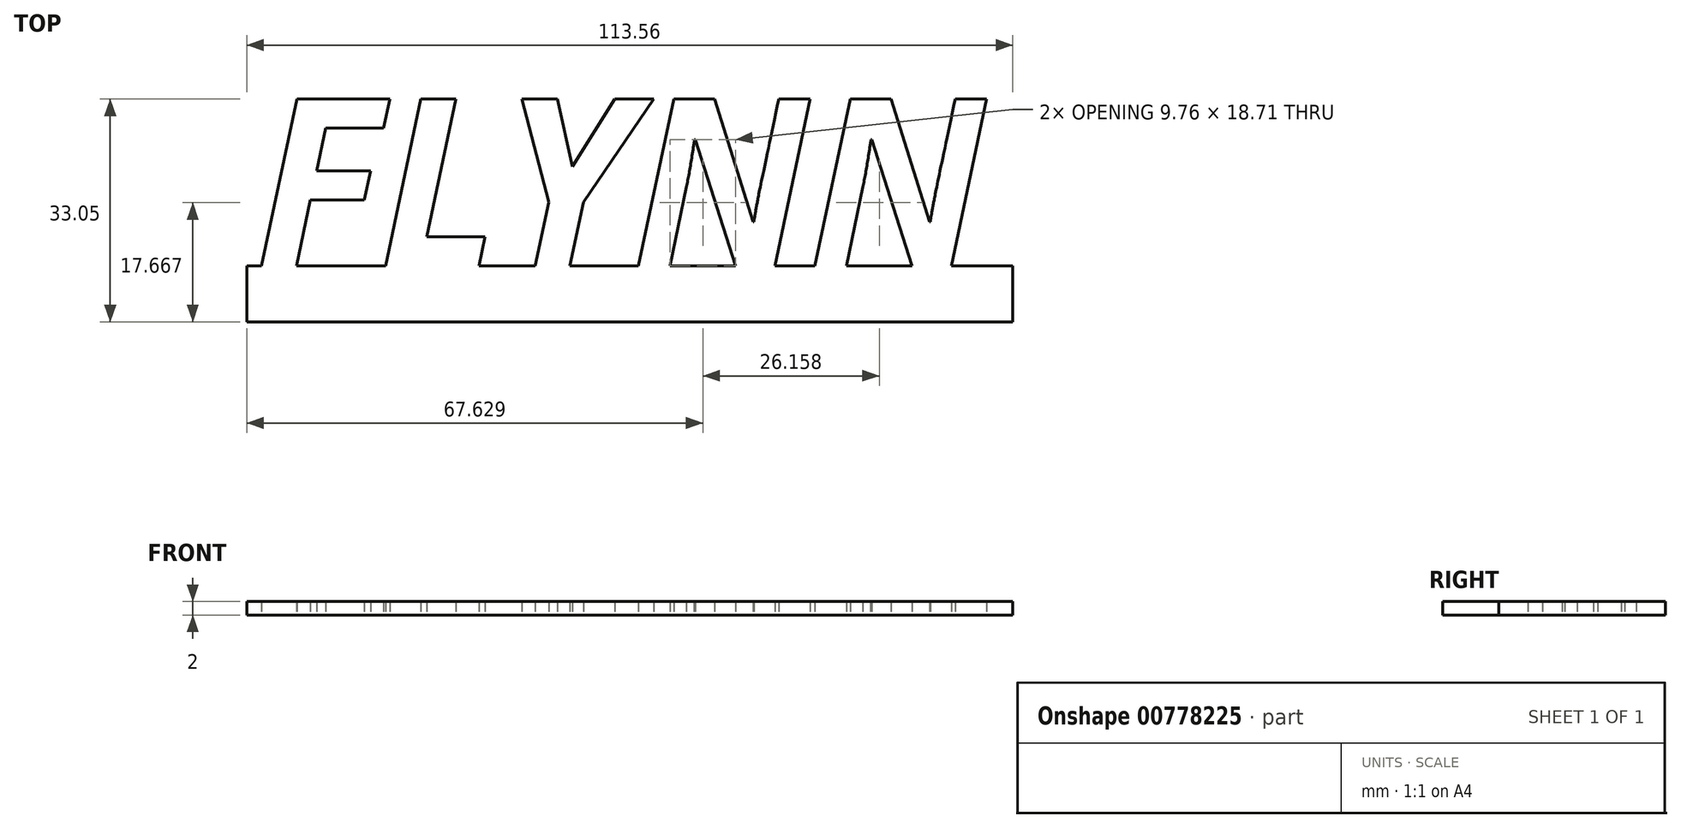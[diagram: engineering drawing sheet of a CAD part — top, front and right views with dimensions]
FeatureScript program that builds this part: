
annotation { "Feature Type Name" : "Feature", "Feature Type Description" : "" }
export const myFeature = defineFeature(function(context is Context, id is Id, definition is map)
    precondition{}
    {
        {
            var Q0;
            Q0=qCreatedBy(makeId("Top.planeOp"),FACE);
            var sketch = newSketch(context, id + "F0", { "sketchPlane" : qUnion([Q0])});
            skLineSegment(sketch, "E0.bottom", {"start": v(-35.84, 13.82) * mm, "end": v(77.72, 13.82) * mm});
            skLineSegment(sketch, "E0.top", {"start": v(-35.84, 5.5) * mm, "end": v(77.72, 5.5) * mm});
            skLineSegment(sketch, "E0.left", {"start": v(-35.84, 13.82) * mm, "end": v(-35.84, 5.5) * mm});
            skLineSegment(sketch, "E0.right", {"start": v(77.72, 13.82) * mm, "end": v(77.72, 5.5) * mm});
            skText(sketch, "E1", { "text": "FLYNN", "fontName": "OpenSans-BoldItalic.ttf"});
            const initialGuessF0  = {"E1": [-0.03453, 0.01382, 1, 0, 0.02495]};
            skSetInitialGuess(sketch, initialGuessF0);
            skSolve(sketch);
        }
        {
            var Q0;
            Q0 = qSketchRegion(id + "F0", true);
            extrude(context, id + "F1", {"entities" : qUnion([Q0]), "depth" : 2 * mm, "offsetDistance" : 25 * mm});
        }
    });
